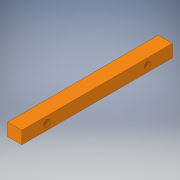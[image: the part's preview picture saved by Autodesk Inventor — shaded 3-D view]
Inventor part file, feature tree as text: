
AUTODESK INVENTOR PART (.ipt)
format: ipt  version: 2019 (Build 230136000, 136)  size: 111,104 bytes
history: native  units: in
note: dims shown in document units (in); Inventor stores cm internally (conversion verified against a paired STEP export)
features: extrude x2, sketch x2
ambient origin geometry x8: Origin, YZ Plane, XZ Plane, XY Plane, X Axis, Y Axis, Z Axis, Center Point
bodies: Solid1 (feature_tree)
feature tree (4):
  extrude  "Extrusion1"  Depth=0.565in
  extrude  "Extrusion2"  Depth=0.5in
  sketch  "Sketch1"  dims[d0=6.0in d1=0.565in]
  sketch  "Sketch2"  dims[d2=0.5in d3=0.0in d4=0.25in d5=0.25in d6=4.0in d7=6.0in d8=1.0in d9=0.5in d10=0.25in d11=0.25in d12=0.5in d13=0.0in]
